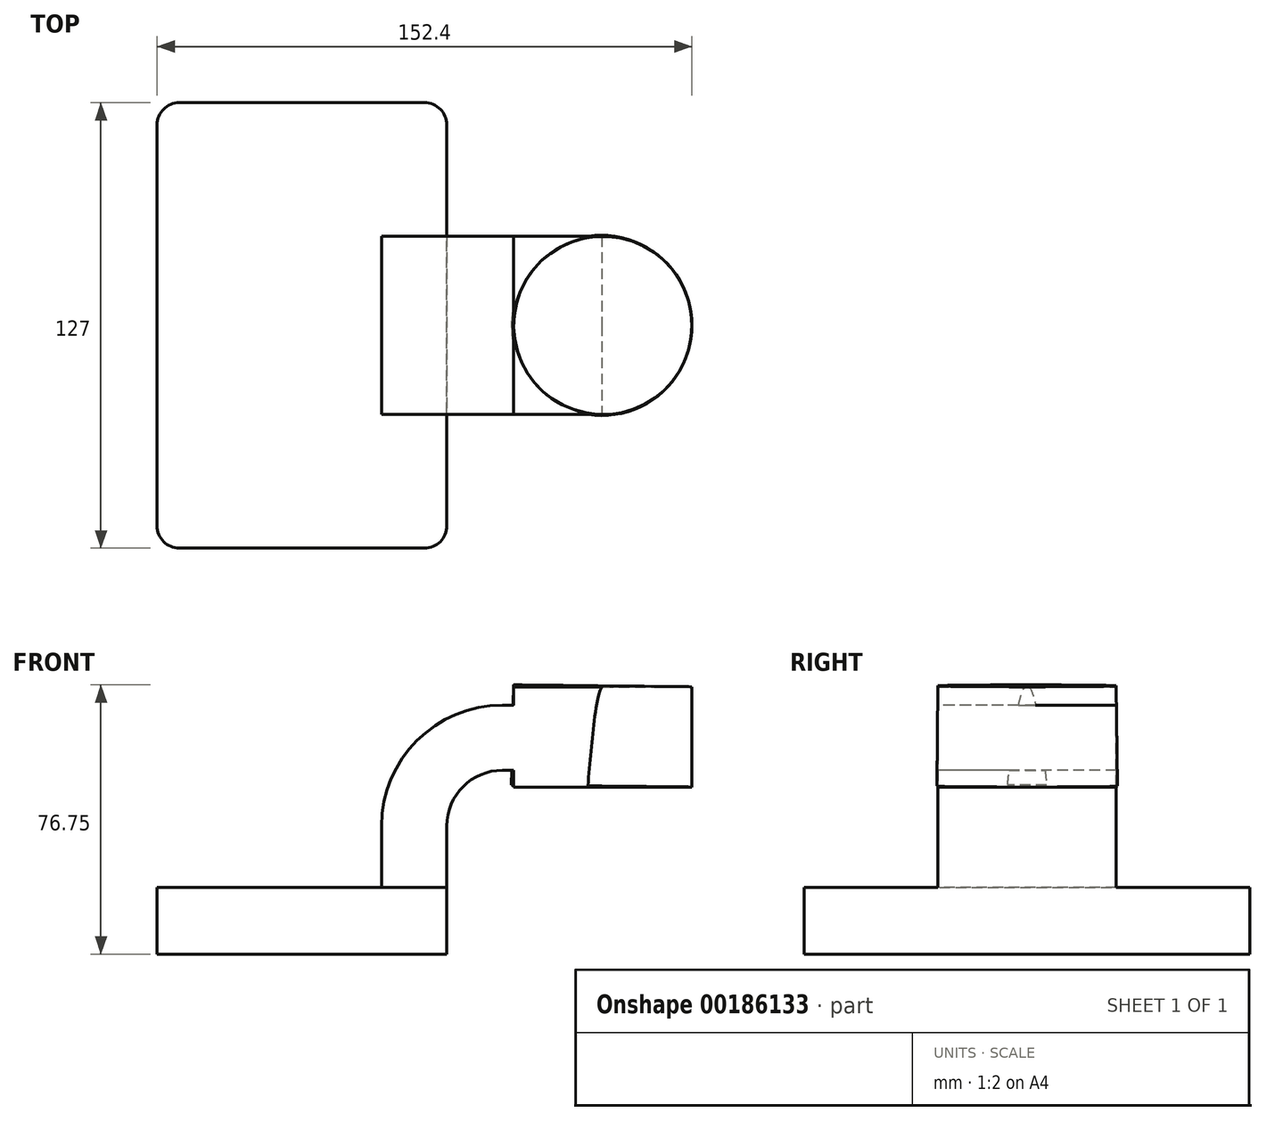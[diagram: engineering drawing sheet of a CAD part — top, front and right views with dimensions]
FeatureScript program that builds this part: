
annotation { "Feature Type Name" : "Feature", "Feature Type Description" : "" }
export const myFeature = defineFeature(function(context is Context, id is Id, definition is map)
    precondition{}
    {
        {
            var Q0;
            Q0=qCreatedBy(makeId("Front.planeOp"),FACE);
            var sketch = newSketch(context, id + "F0", { "sketchPlane" : qUnion([Q0])});
            skLineSegment(sketch, "E0.bottom", {"start": v(-41.28, 9.52) * mm, "end": v(41.28, 9.53) * mm});
            skLineSegment(sketch, "E0.top", {"start": v(-41.27, -9.53) * mm, "end": v(41.28, -9.53) * mm});
            skLineSegment(sketch, "E0.left", {"start": v(-41.28, 9.52) * mm, "end": v(-41.28, -9.53) * mm});
            skLineSegment(sketch, "E0.right", {"start": v(41.27, 9.53) * mm, "end": v(41.28, -9.52) * mm});
            skPoint(sketch, "E0.middle", {"position": v(0, 0) * mm});
            skLineSegment(sketch, "E1.bottom", {"start": v(60.32, 38.1) * mm, "end": v(111.12, 38.1) * mm});
            skLineSegment(sketch, "E1.top", {"start": v(60.32, 66.67) * mm, "end": v(111.12, 66.67) * mm});
            skLineSegment(sketch, "E1.left", {"start": v(60.32, 38.1) * mm, "end": v(60.32, 66.68) * mm});
            skLineSegment(sketch, "E1.right", {"start": v(111.12, 38.1) * mm, "end": v(111.12, 66.68) * mm});
            skPoint(sketch, "E1.middle", {"position": v(85.72, 52.39) * mm});
            skLineSegment(sketch, "E2", {"start": v(41.28, 9.53) * mm, "end": v(41.28, 27) * mm});
            skArc(sketch, "E3", {"start": v(41.27, 27) * mm, "mid": v(45.92, 38.23) * mm, "end": v(57.15, 42.88) * mm});
            skLineSegment(sketch, "E4", {"start": v(57.15, 42.88) * mm, "end": v(85.47, 42.88) * mm});
            skLineSegment(sketch, "E5.0", {"start": v(57.15, 61.46) * mm, "end": v(85.42, 61.46) * mm});
            skArc(sketch, "E5.1", {"start": v(22.7, 27) * mm, "mid": v(32.78, 51.37) * mm, "end": v(57.15, 61.46) * mm});
            skLineSegment(sketch, "E5.2", {"start": v(22.7, 9.53) * mm, "end": v(22.7, 27) * mm});
            skFitSpline(sketch, "E6", {"points": [v(-41.28, 9.52) * mm, v(57.15, 61.46) * mm], "startDerivative": vector(1.61, 84.87) * mm, "endDerivative": vector(135.92, -3.68) * mm});
            skLineSegment(sketch, "E7", {"start": v(85.72, 66.67) * mm, "end": v(85.42, 38.1) * mm});
            skSolve(sketch);
        }
        {
            var Q0;
            Q0=makeQuery(id+"F0.imprint","IMPRINT",FACE,{"disambiguationData":[TD([[makeQuery(id+"F0.imprint","IMPRINT",EDGE,{"derivedFrom":sQuery(id+"F0.wireOp",EDGE,"E0.top")}),1.0]])]});
            extrude(context, id + "F1", {"entities" : qUnion([Q0]), "endBound" : BoundingType.SYMMETRIC, "depth" : 127 * mm});
        }
        {
            var Q0;
            {var subQ2=sQuery(id+"F0.wireOp",EDGE,"E2");Q0=makeQuery(id+"F0.imprint","IMPRINT",FACE,{"disambiguationData":[TD([[makeQuery(id+"F0.imprint","IMPRINT",EDGE,{"derivedFrom":subQ2}),1.0]])]});}
            var Q1;
            {var subQ3=sQuery(id+"F0.wireOp",EDGE,"E1.left");var subQ5=sQuery(id+"F0.wireOp",EDGE,"E1.top");var subQ6=makeQuery(id+"F0.imprint","INTERSECT",VERTEX,{"derivedFrom":[subQ5,subQ3]});Q1=makeQuery(id+"F0.imprint","IMPRINT",FACE,{"disambiguationData":[TD([[makeQuery(id+"F0.imprint","IMPRINT",EDGE,{"disambiguationData":[TD([[subQ6,-1.0]])],"derivedFrom":subQ5}),-1.0]])]});}
            var Q2;
            {var subQ0=sQuery(id+"F0.wireOp",EDGE,"E1.left");var subQ1=sQuery(id+"F0.wireOp",EDGE,"E1.bottom");var subQ2=makeQuery(id+"F0.imprint","INTERSECT",VERTEX,{"derivedFrom":[subQ1,subQ0]});Q2=makeQuery(id+"F0.imprint","IMPRINT",FACE,{"disambiguationData":[TD([[makeQuery(id+"F0.imprint","IMPRINT",EDGE,{"disambiguationData":[TD([[subQ2,-1.0]])],"derivedFrom":subQ1}),1.0]])]});}
            extrude(context, id + "F2", {"entities" : qUnion([Q0, Q1, Q2]), "operationType" : NewBodyOperationType.ADD, "endBound" : BoundingType.SYMMETRIC, "oppositeDirection" : true, "depth" : 50.8 * mm});
        }
        {
            var Q0;
            Q0=makeQuery(id+"F0.imprint","IMPRINT",FACE,{"disambiguationData":[TD([[makeQuery(id+"F0.imprint","IMPRINT",EDGE,{"derivedFrom":sQuery(id+"F0.wireOp",EDGE,"E5.1")}),1.0]])]});
            extrude(context, id + "F3", {"entities" : qUnion([Q0]), "operationType" : NewBodyOperationType.ADD, "endBound" : BoundingType.SYMMETRIC, "depth" : 15.88 * mm});
        }
        {
            var Q0;
            {var subQ0=sQuery(id+"F0.wireOp",EDGE,"E1.right");Q0=makeQuery(id+"F0.imprint","IMPRINT",FACE,{"disambiguationData":[TD([[makeQuery(id+"F0.imprint","IMPRINT",EDGE,{"derivedFrom":subQ0}),1.0]])]});}
            var Q1;
            Q1=sQuery(id+"F0.wireOp",EDGE,"E7");
            revolve(context, id + "F4", {"operationType" : NewBodyOperationType.ADD, "entities" : qUnion([Q0]), "axis" : qUnion([Q1]), "revolveType" : RevolveType.FULL});
        }
        {
            var Q0;
            Q0=makeQuery(id+"F1.opExtrude","CAP_EDGE",EDGE,{"disambiguationData":[OSD([sQuery(id+"F0.wireOp",EDGE,"E0.right")])],"isStart":true});
            var Q1;
            Q1=makeQuery(id+"F1.opExtrude","CAP_EDGE",EDGE,{"disambiguationData":[OSD([sQuery(id+"F0.wireOp",EDGE,"E0.left")])],"isStart":true});
            var Q2;
            Q2=makeQuery(id+"F1.opExtrude","CAP_EDGE",EDGE,{"disambiguationData":[OSD([sQuery(id+"F0.wireOp",EDGE,"E0.left")])],"isStart":false});
            var Q3;
            Q3=makeQuery(id+"F1.opExtrude","CAP_EDGE",EDGE,{"disambiguationData":[OSD([sQuery(id+"F0.wireOp",EDGE,"E0.right")])],"isStart":false});
            fillet(context, id + "F5", {"entities" : qUnion([Q0, Q1, Q2, Q3]), "radius" : 6.35 * mm, "tangentPropagation" : true, "allowEdgeOverflow" : false});
        }
    });
